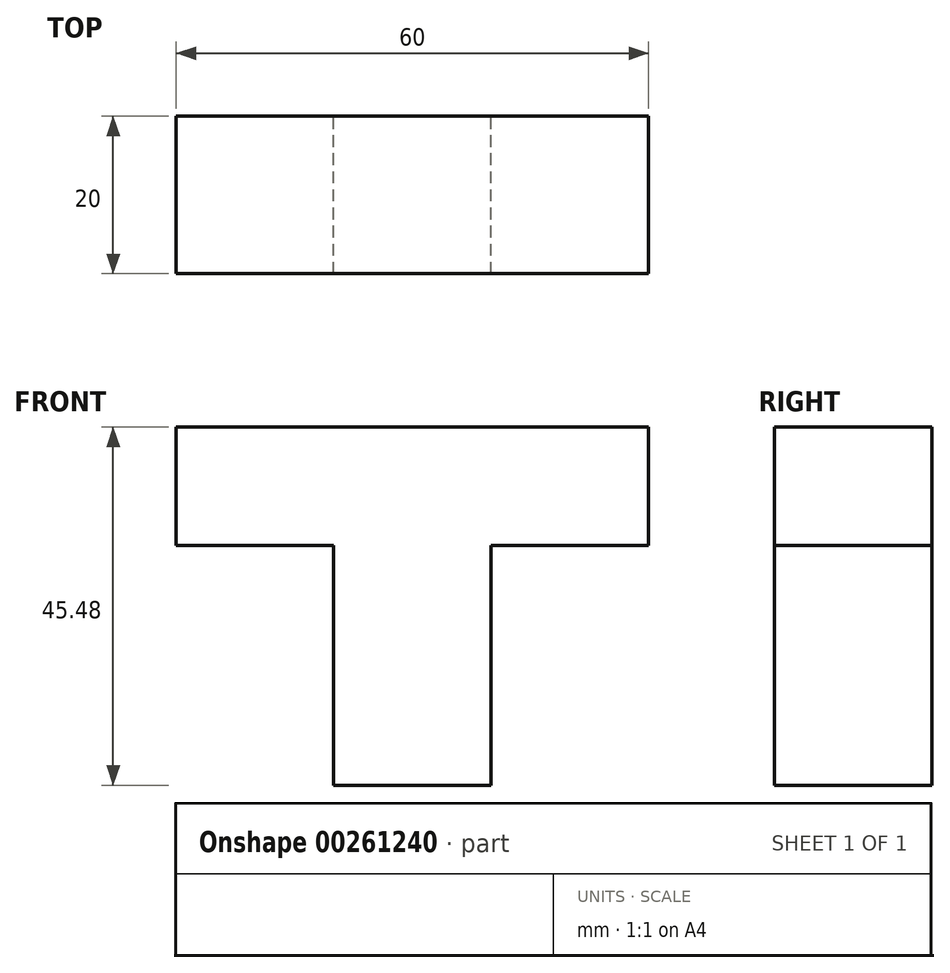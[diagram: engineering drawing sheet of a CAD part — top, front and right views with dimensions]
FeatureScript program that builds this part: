
annotation { "Feature Type Name" : "Feature", "Feature Type Description" : "" }
export const myFeature = defineFeature(function(context is Context, id is Id, definition is map)
    precondition{}
    {
        {
            var Q0;
            Q0=qCreatedBy(makeId("Front.planeOp"),FACE);
            var sketch = newSketch(context, id + "F0", { "sketchPlane" : qUnion([Q0])});
            skLineSegment(sketch, "E0", {"start": v(22.28, 39.57) * mm, "end": v(-37.72, 39.57) * mm});
            skLineSegment(sketch, "E1", {"start": v(-37.72, 39.57) * mm, "end": v(-37.72, 24.57) * mm});
            skLineSegment(sketch, "E2", {"start": v(-37.72, 24.57) * mm, "end": v(-17.72, 24.57) * mm});
            skLineSegment(sketch, "E3", {"start": v(-17.72, 24.57) * mm, "end": v(-17.72, -5.9) * mm});
            skLineSegment(sketch, "E4", {"start": v(-17.72, -5.9) * mm, "end": v(2.28, -5.9) * mm});
            skLineSegment(sketch, "E5", {"start": v(2.28, -5.9) * mm, "end": v(2.28, 24.57) * mm});
            skLineSegment(sketch, "E6", {"start": v(2.28, 24.57) * mm, "end": v(22.28, 24.57) * mm});
            skLineSegment(sketch, "E7", {"start": v(22.28, 24.57) * mm, "end": v(22.28, 39.57) * mm});
            skSolve(sketch);
        }
        {
            var Q0;
            Q0 = qSketchRegion(id + "F0", true);
            extrude(context, id + "F1", {"entities" : qUnion([Q0]), "depth" : 20 * mm});
        }
    });
